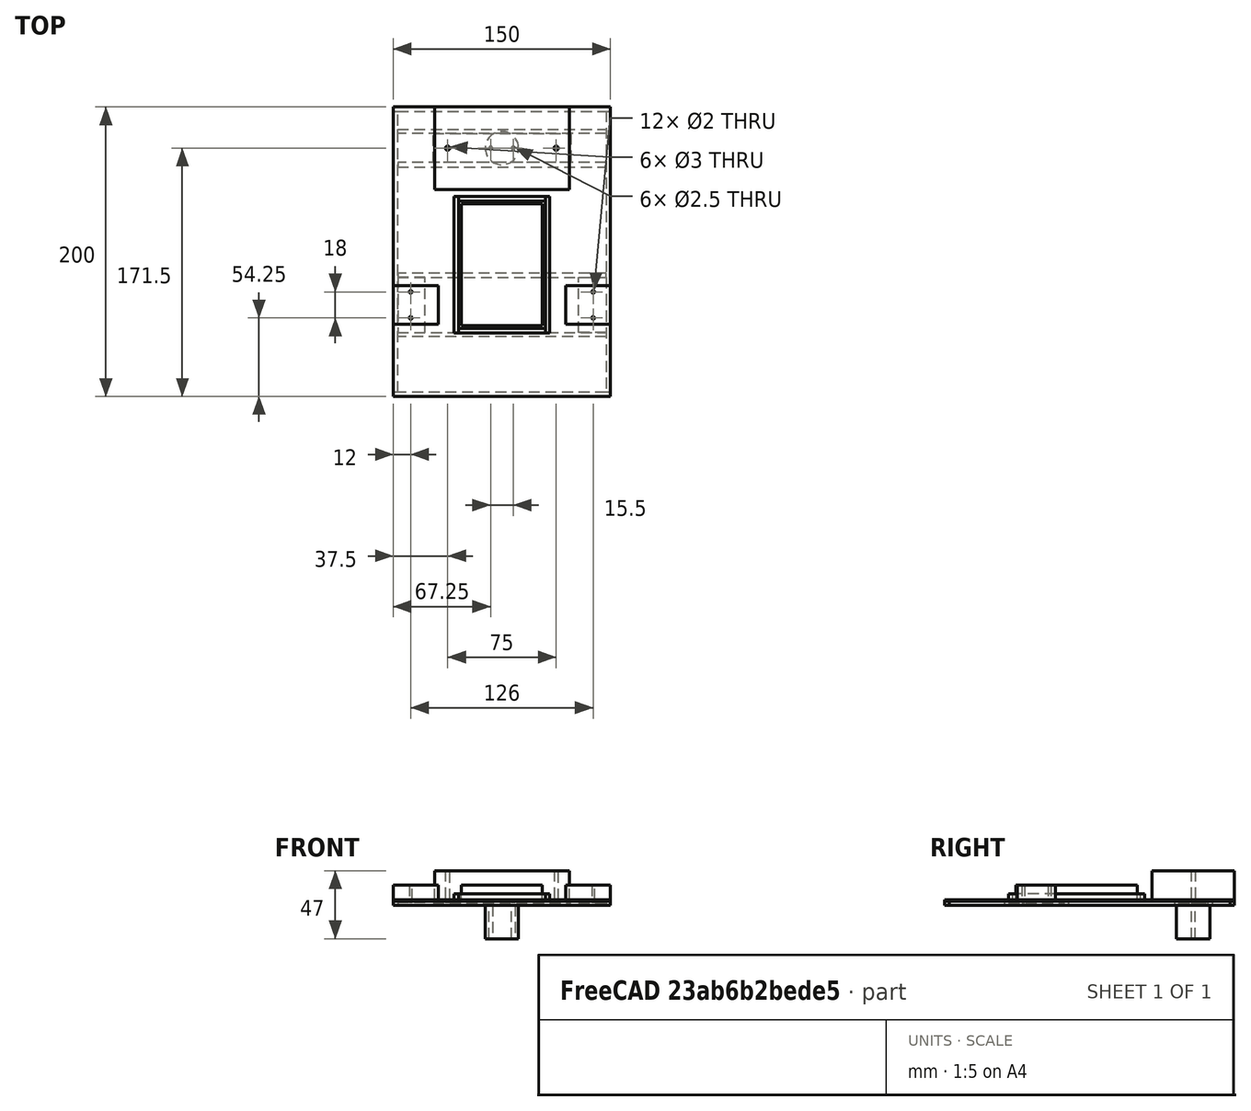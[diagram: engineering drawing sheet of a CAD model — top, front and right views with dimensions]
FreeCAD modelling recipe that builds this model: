
FCSTD DOCUMENT  (FreeCAD 0.20R26375 (Git))
Label: Robot
License: All rights reserved
LicenseURL: http://en.wikipedia.org/wiki/All_rights_reserved
objects: PartDesign::ShapeBinder×23, PartDesign::Pad×21, PartDesign::Body×21, TechDraw::DrawViewDimension×11, Sketcher::SketchObject×7, TechDraw::DrawProjGroupItem×5, TechDraw::DrawProjGroup×5, PartDesign::Pocket×3, TechDraw::DrawSVGTemplate×2, TechDraw::DrawPage×2
note: 99 computed .brp shape members not serialized (recipe doc carries the construction recipe); baked Part::Feature solids carry a one-line shape summary decoded from their .brp

FEATURE [Sketcher::SketchObject] Sketch  label="ChassisOutline"
  FullyConstrained = true
  MapMode = 5
  Support = -> [XY_Plane]
  sketch-geometry (4):
    g0: LineSegment StartX=-75 StartY=100 StartZ=0 EndX=75 EndY=100 EndZ=0
    g1: LineSegment StartX=75 StartY=100 StartZ=0 EndX=75 EndY=-100 EndZ=0
    g2: LineSegment StartX=75 StartY=-100 StartZ=0 EndX=-75 EndY=-100 EndZ=0
    g3: LineSegment StartX=-75 StartY=-100 StartZ=0 EndX=-75 EndY=100 EndZ=0
  constraints (11):
    c: Coincident(g0,g1)
    c: Coincident(g1,g2)
    c: Coincident(g2,g3)
    c: Coincident(g3,g0)
    c: Horizontal(g0)
    c: Horizontal(g2)
    c: Vertical(g1)
    c: Vertical(g3)
    c: Distance(g0) = 150
    c: Distance(g3) = 200
    c: Symmetric(g0,g1,g-1)
FEATURE [Sketcher::SketchObject] Sketch001  label="UpperParts"
  ExternalGeometry = -> [Sketch]
  FullyConstrained = true
  MapMode = 5
  Support = -> [XY_Plane]
  sketch-geometry (24):
    g0: LineSegment StartX=-46.5 StartY=100 StartZ=0 EndX=46.5 EndY=100 EndZ=0
    g1: LineSegment StartX=46.5 StartY=100 StartZ=0 EndX=46.5 EndY=43 EndZ=0
    g2: LineSegment StartX=46.5 StartY=43 StartZ=0 EndX=-46.5 EndY=43 EndZ=0
    g3: LineSegment StartX=-46.5 StartY=43 StartZ=0 EndX=-46.5 EndY=100 EndZ=0
    g4: LineSegment StartX=-28 StartY=33 StartZ=0 EndX=28 EndY=33 EndZ=0
    g5: LineSegment StartX=28 StartY=33 StartZ=0 EndX=28 EndY=-51 EndZ=0
    g6: LineSegment StartX=28 StartY=-51 StartZ=0 EndX=-28 EndY=-51 EndZ=0
    g7: LineSegment StartX=-28 StartY=-51 StartZ=0 EndX=-28 EndY=33 EndZ=0
    g8: LineSegment StartX=-44 StartY=-50 StartZ=0 EndX=-75 EndY=-50 EndZ=0
    g9: LineSegment StartX=-75 StartY=-50 StartZ=0 EndX=-75 EndY=-23.5 EndZ=0
    g10: LineSegment StartX=-75 StartY=-23.5 StartZ=0 EndX=-44 EndY=-23.5 EndZ=0
    g11: LineSegment StartX=-44 StartY=-23.5 StartZ=0 EndX=-44 EndY=-50 EndZ=0
    g12: LineSegment StartX=75 StartY=-23.5 StartZ=0 EndX=44 EndY=-23.5 EndZ=0
    g13: LineSegment StartX=44 StartY=-23.5 StartZ=0 EndX=44 EndY=-50 EndZ=0
    g14: LineSegment StartX=44 StartY=-50 StartZ=0 EndX=75 EndY=-50 EndZ=0
    g15: LineSegment StartX=75 StartY=-50 StartZ=0 EndX=75 EndY=-23.5 EndZ=0
    g16: LineSegment StartX=-37.5 StartY=71.5 StartZ=0 EndX=0 EndY=71.5 EndZ=0
    g17: Circle CenterX=-37.5 CenterY=71.5 CenterZ=0 NormalX=0 NormalY=0 NormalZ=1 AngleXU=0 Radius=1.5
    g18: Circle CenterX=37.5 CenterY=71.5 CenterZ=0 NormalX=0 NormalY=0 NormalZ=1 AngleXU=0 Radius=1.5
    g19: Circle CenterX=-63 CenterY=-27.75 CenterZ=0 NormalX=0 NormalY=0 NormalZ=1 AngleXU=0 Radius=1
    g20: Circle CenterX=-63 CenterY=-45.75 CenterZ=0 NormalX=0 NormalY=0 NormalZ=1 AngleXU=0 Radius=1
    g21: Circle CenterX=63 CenterY=-27.75 CenterZ=0 NormalX=0 NormalY=0 NormalZ=1 AngleXU=0 Radius=1
    g22: Circle CenterX=63 CenterY=-45.75 CenterZ=0 NormalX=0 NormalY=0 NormalZ=1 AngleXU=0 Radius=1
    g23: LineSegment StartX=-75 StartY=-36.75 StartZ=0 EndX=-44 EndY=-36.75 EndZ=0
  constraints (64):
    c: Coincident(g0,g1)
    c: Coincident(g1,g2)
    c: Coincident(g2,g3)
    c: Coincident(g3,g0)
    c: Horizontal(g0)
    c: Vertical(g1)
    c: Vertical(g3)
    c: PointOnObject(g0,g-3)
    c: Symmetric(g2,g1,g-2)
    c: Distance(g2) = 93
    c: Distance(g3) = 57
    c: Coincident(g4,g5)
    c: Coincident(g5,g6)
    c: Coincident(g6,g7)
    c: Coincident(g7,g4)
    c: Horizontal(g6)
    c: Vertical(g5)
    c: Vertical(g7)
    c: Symmetric(g4,g4,g-2)
    c: Distance(g4) = 56
    c: Distance(g7) = 84
    c: DistanceY(g4,g2) = 10
    c: Coincident(g8,g9)
    c: Coincident(g9,g10)
    c: Coincident(g10,g11)
    c: Coincident(g11,g8)
    c: Horizontal(g8)
    c: Horizontal(g10)
    c: Vertical(g9)
    c: Vertical(g11)
    c: PointOnObject(g9,g-4)
    c: Coincident(g12,g13)
    c: Coincident(g13,g14)
    c: Coincident(g14,g15)
    c: Coincident(g15,g12)
    c: Horizontal(g12)
    c: Horizontal(g14)
    c: Vertical(g13)
    c: Vertical(g15)
    c: PointOnObject(g12,g-6)
    c: Symmetric(g10,g12,g-2)
    c: Equal(g11,g13)
    c: Distance(g9) = 26.5
    c: Distance(g10) = 31
    c: Distance(g8,g-5) = 50
    c: PointOnObject(g16,g-2)
    c: Coincident(g17,g16)
    c: DistanceX(g17,g18) = 75
    c: Equal(g17,g18)
    c: Symmetric(g17,g18,g-2)
    c: Diameter(g18) = 3
    c: Symmetric(g0,g2,g16)
    c: PointOnObject(g23,g9)
    c: PointOnObject(g23,g11)
    c: Symmetric(g19,g20,g23)
    c: Distance(g20,g19) = 18
    c: Symmetric(g8,g9,g23)
    c: Symmetric(g20,g22,g-2)
    c: Symmetric(g19,g21,g-2)
    c: Equal(g21,g22)
    c: Equal(g22,g20)
    c: Equal(g20,g19)
    c: Diameter(g19) = 2
    c: DistanceX(g9,g19) = 12
FEATURE [PartDesign::Pad] Pad
  Direction = (0,0,1)
  Length = 1
  Length2 = 100
  Profile = -> Sketch
  Reversed = true
  Type = 0
FEATURE [PartDesign::ShapeBinder] ShapeBinder
  Support = -> [Sketch001]
  TraceSupport = false
FEATURE [PartDesign::Pocket] Pocket
  BaseFeature = -> Pad
  Direction = (1,1,1)
  Length = 5
  Length2 = 100
  Profile = -> ShapeBinder
  Type = 1
FEATURE [PartDesign::ShapeBinder] ShapeBinder001
  Support = -> [Sketch001]
  TraceSupport = false
FEATURE [PartDesign::Pad] Pad001
  Direction = (0,0,-1)
  Length = 20
  Length2 = 100
  Profile = -> ShapeBinder001
  Reversed = true
  Type = 0
FEATURE [PartDesign::Body] Body001  label="BatteryBox"
  Group = -> [ShapeBinder001,Pad001]
  Origin = -> Origin001
  Tip = -> Pad001
FEATURE [PartDesign::ShapeBinder] ShapeBinder002
  Support = -> [Sketch001]
  TraceSupport = false
FEATURE [PartDesign::Pad] Pad002
  Direction = (0,0,-1)
  Length = 10
  Length2 = 100
  Profile = -> ShapeBinder002
  Reversed = true
  Type = 0
FEATURE [PartDesign::Body] Body002  label="Breadboard"
  Group = -> [ShapeBinder002,Pad002]
  Origin = -> Origin002
  Tip = -> Pad002
FEATURE [PartDesign::ShapeBinder] ShapeBinder003
  Support = -> [Sketch001]
  TraceSupport = false
FEATURE [PartDesign::Pad] Pad003
  Direction = (0,0,-1)
  Length = 10
  Length2 = 100
  Profile = -> ShapeBinder003
  Reversed = true
  Type = 0
FEATURE [PartDesign::Body] Body003  label="LeftMotor"
  Group = -> [ShapeBinder003,Pad003]
  Origin = -> Origin003
  Tip = -> Pad003
FEATURE [PartDesign::ShapeBinder] ShapeBinder004
  Support = -> [Sketch001]
  TraceSupport = false
FEATURE [PartDesign::Pad] Pad004
  Direction = (0,0,1)
  Length = 10
  Length2 = 100
  Profile = -> ShapeBinder004
  Type = 0
FEATURE [PartDesign::Body] Body004  label="RightMotor"
  Group = -> [ShapeBinder004,Pad004]
  Origin = -> Origin004
  Tip = -> Pad004
FEATURE [Sketcher::SketchObject] Sketch002  label="OuterSupportRods"
  ExternalGeometry = -> [Pocket]
  FullyConstrained = true
  MapMode = 5
  Placement = pos=(0,0,-1) rot=(1,0,0;3.14159rad)
  Support = -> [Pocket]
  sketch-geometry (16):
    g0: LineSegment StartX=-75 StartY=100 StartZ=0 EndX=75 EndY=100 EndZ=0
    g1: LineSegment StartX=75 StartY=100 StartZ=0 EndX=75 EndY=97 EndZ=0
    g2: LineSegment StartX=-75 StartY=97 StartZ=0 EndX=-75 EndY=100 EndZ=0
    g3: LineSegment StartX=75 StartY=-100 StartZ=0 EndX=-75 EndY=-100 EndZ=0
    g4: LineSegment StartX=-75 StartY=-100 StartZ=0 EndX=-75 EndY=-97 EndZ=0
    g5: LineSegment StartX=75 StartY=-97 StartZ=0 EndX=75 EndY=-100 EndZ=0
    g6: LineSegment StartX=-72 StartY=97 StartZ=0 EndX=-75 EndY=97 EndZ=0
    g7: LineSegment StartX=75 StartY=97 StartZ=0 EndX=72 EndY=97 EndZ=0
    g8: LineSegment StartX=72 StartY=97 StartZ=0 EndX=-72 EndY=97 EndZ=0
    g9: LineSegment StartX=72 StartY=-97 StartZ=0 EndX=75 EndY=-97 EndZ=0
    g10: LineSegment StartX=-75 StartY=-97 StartZ=0 EndX=-72 EndY=-97 EndZ=0
    g11: LineSegment StartX=-72 StartY=-97 StartZ=0 EndX=72 EndY=-97 EndZ=0
    g12: LineSegment StartX=-75 StartY=97 StartZ=0 EndX=-75 EndY=-97 EndZ=0
    g13: LineSegment StartX=75 StartY=97 StartZ=0 EndX=75 EndY=-97 EndZ=0
    g14: LineSegment StartX=72 StartY=-97 StartZ=0 EndX=72 EndY=97 EndZ=0
    g15: LineSegment StartX=-72 StartY=97 StartZ=0 EndX=-72 EndY=-97 EndZ=0
  constraints (40):
    c: Coincident(g0,g1)
    c: Coincident(g1,g7)
    c: Coincident(g6,g2)
    c: Coincident(g2,g0)
    c: Vertical(g1)
    c: Vertical(g2)
    c: Coincident(g3,g4)
    c: Coincident(g4,g10)
    c: Coincident(g9,g5)
    c: Coincident(g5,g3)
    c: Vertical(g4)
    c: Vertical(g5)
    c: Equal(g2,g4)
    c: Distance(g2) = 3
    c: Coincident(g3,g-3)
    c: Coincident(g0,g-3)
    c: Coincident(g-4,g0)
    c: Coincident(g3,g-4)
    c: Coincident(g8,g6)
    c: Horizontal(g6)
    c: Coincident(g7,g8)
    c: Horizontal(g7)
    c: Horizontal(g8)
    c: Coincident(g11,g9)
    c: Horizontal(g9)
    c: Coincident(g10,g11)
    c: Horizontal(g10)
    c: Horizontal(g11)
    c: Equal(g6,g7)
    c: Equal(g6,g2)
    c: Coincident(g12,g2)
    c: Coincident(g12,g4)
    c: Coincident(g13,g1)
    c: Coincident(g13,g5)
    c: Coincident(g14,g9)
    c: Coincident(g14,g7)
    c: Coincident(g15,g6)
    c: Coincident(g15,g10)
    c: Vertical(g15)
    c: Vertical(g14)
FEATURE [PartDesign::ShapeBinder] ShapeBinder005
  Support = -> [Sketch002]
  TraceSupport = false
FEATURE [PartDesign::Pad] Pad005
  Direction = (0,0,1)
  Length = 3
  Length2 = 100
  Profile = -> ShapeBinder005
  Reversed = true
  Type = 0
FEATURE [PartDesign::Body] Body005  label="FrontRod"
  Group = -> [ShapeBinder005,Pad005]
  Origin = -> Origin005
  Tip = -> Pad005
FEATURE [PartDesign::ShapeBinder] ShapeBinder006
  Support = -> [Sketch002]
  TraceSupport = false
FEATURE [PartDesign::Pad] Pad006
  Direction = (0,0,1)
  Length = 3
  Length2 = 100
  Profile = -> ShapeBinder006
  Reversed = true
  Type = 0
FEATURE [PartDesign::Body] Body006  label="RearRod"
  Group = -> [ShapeBinder006,Pad006]
  Origin = -> Origin006
  Tip = -> Pad006
FEATURE [PartDesign::ShapeBinder] ShapeBinder007
  Support = -> [Sketch002]
  TraceSupport = false
FEATURE [PartDesign::Pad] Pad007
  Direction = (0,0,-1)
  Length = 3
  Length2 = 100
  Profile = -> ShapeBinder007
  Type = 0
FEATURE [PartDesign::Body] Body007  label="LeftRod"
  Group = -> [ShapeBinder007,Pad007]
  Origin = -> Origin007
  Tip = -> Pad007
FEATURE [PartDesign::ShapeBinder] ShapeBinder008
  Support = -> [Sketch002]
  TraceSupport = false
FEATURE [PartDesign::Pad] Pad008
  Direction = (0,0,1)
  Length = 3
  Length2 = 100
  Profile = -> ShapeBinder008
  Reversed = true
  Type = 0
FEATURE [PartDesign::Body] Body008  label="RightRod"
  Group = -> [ShapeBinder008,Pad008]
  Origin = -> Origin008
  Tip = -> Pad008
FEATURE [Sketcher::SketchObject] Sketch003  label="InnerSupportRods"
  ExternalGeometry = -> [Sketch002,Pocket]
  FullyConstrained = true
  MapMode = 5
  Placement = pos=(0,0,-1) rot=(1,0,0;3.14159rad)
  Support = -> [Pocket]
  sketch-geometry (16):
    g0: LineSegment StartX=-72 StartY=55.75 StartZ=0 EndX=72 EndY=55.75 EndZ=0
    g1: LineSegment StartX=72 StartY=55.75 StartZ=0 EndX=72 EndY=58.75 EndZ=0
    g2: LineSegment StartX=72 StartY=58.75 StartZ=0 EndX=-72 EndY=58.75 EndZ=0
    g3: LineSegment StartX=-72 StartY=58.75 StartZ=0 EndX=-72 EndY=55.75 EndZ=0
    g4: LineSegment StartX=-72 StartY=17.75 StartZ=0 EndX=72 EndY=17.75 EndZ=0
    g5: LineSegment StartX=72 StartY=17.75 StartZ=0 EndX=72 EndY=14.75 EndZ=0
    g6: LineSegment StartX=72 StartY=14.75 StartZ=0 EndX=-72 EndY=14.75 EndZ=0
    g7: LineSegment StartX=-72 StartY=14.75 StartZ=0 EndX=-72 EndY=17.75 EndZ=0
    g8: LineSegment StartX=-72 StartY=-58.5 StartZ=0 EndX=72 EndY=-58.5 EndZ=0
    g9: LineSegment StartX=72 StartY=-58.5 StartZ=0 EndX=72 EndY=-61.5 EndZ=0
    g10: LineSegment StartX=72 StartY=-61.5 StartZ=0 EndX=-72 EndY=-61.5 EndZ=0
    g11: LineSegment StartX=-72 StartY=-61.5 StartZ=0 EndX=-72 EndY=-58.5 EndZ=0
    g12: LineSegment StartX=72 StartY=-81.5 StartZ=0 EndX=-72 EndY=-81.5 EndZ=0
    g13: LineSegment StartX=-72 StartY=-81.5 StartZ=0 EndX=-72 EndY=-84.5 EndZ=0
    g14: LineSegment StartX=-72 StartY=-84.5 StartZ=0 EndX=72 EndY=-84.5 EndZ=0
    g15: LineSegment StartX=72 StartY=-84.5 StartZ=0 EndX=72 EndY=-81.5 EndZ=0
  constraints (48):
    c: Coincident(g0,g1)
    c: Coincident(g1,g2)
    c: Coincident(g2,g3)
    c: Coincident(g3,g0)
    c: Horizontal(g0)
    c: Horizontal(g2)
    c: Vertical(g1)
    c: Vertical(g3)
    c: PointOnObject(g0,g-4)
    c: PointOnObject(g1,g-5)
    c: Coincident(g4,g5)
    c: Coincident(g5,g6)
    c: Coincident(g6,g7)
    c: Coincident(g7,g4)
    c: Horizontal(g4)
    c: Horizontal(g6)
    c: Vertical(g5)
    c: Vertical(g7)
    c: PointOnObject(g4,g-4)
    c: PointOnObject(g5,g-5)
    c: Coincident(g8,g9)
    c: Coincident(g9,g10)
    c: Coincident(g10,g11)
    c: Coincident(g11,g8)
    c: Horizontal(g8)
    c: Horizontal(g10)
    c: Vertical(g9)
    c: Vertical(g11)
    c: PointOnObject(g8,g-4)
    c: PointOnObject(g9,g-5)
    c: Coincident(g12,g13)
    c: Coincident(g13,g14)
    c: Coincident(g14,g15)
    c: Coincident(g15,g12)
    c: Horizontal(g12)
    c: Horizontal(g14)
    c: Vertical(g13)
    c: Vertical(g15)
    c: PointOnObject(g12,g-5)
    c: PointOnObject(g13,g-4)
    c: Equal(g13,g11)
    c: Equal(g11,g7)
    c: Equal(g7,g3)
    c: Equal(g3,g-3)
    c: DistanceY(g-8,g0) = 10
    c: DistanceY(g4,g-9) = 10
    c: DistanceY(g-10,g10) = 10
    c: DistanceY(g12,g-10) = 10
FEATURE [Sketcher::SketchObject] Sketch004  label="SupportPlates"
  ExternalGeometry = -> [Sketch002,Sketch003,Pocket]
  FullyConstrained = true
  MapMode = 5
  Placement = pos=(0,0,-1) rot=(1,0,0;3.14159rad)
  Support = -> [Pocket]
  sketch-geometry (18):
    g0: Circle CenterX=-63 CenterY=45.75 CenterZ=0 NormalX=0 NormalY=0 NormalZ=1 AngleXU=0 Radius=1
    g1: Circle CenterX=-63 CenterY=27.75 CenterZ=0 NormalX=0 NormalY=0 NormalZ=1 AngleXU=0 Radius=1
    g2: Circle CenterX=63 CenterY=45.75 CenterZ=0 NormalX=0 NormalY=0 NormalZ=1 AngleXU=0 Radius=1
    g3: Circle CenterX=63 CenterY=27.75 CenterZ=0 NormalX=0 NormalY=0 NormalZ=1 AngleXU=0 Radius=1
    g4: Circle CenterX=-37.5 CenterY=-71.5 CenterZ=0 NormalX=0 NormalY=0 NormalZ=1 AngleXU=0 Radius=1.5
    g5: Circle CenterX=37.5 CenterY=-71.5 CenterZ=0 NormalX=0 NormalY=0 NormalZ=1 AngleXU=0 Radius=1.5
    g6: LineSegment StartX=-72 StartY=55.75 StartZ=0 EndX=-53 EndY=55.75 EndZ=0
    g7: LineSegment StartX=-53 StartY=55.75 StartZ=0 EndX=-53 EndY=17.75 EndZ=0
    g8: LineSegment StartX=-53 StartY=17.75 StartZ=0 EndX=-72 EndY=17.75 EndZ=0
    g9: LineSegment StartX=-72 StartY=17.75 StartZ=0 EndX=-72 EndY=55.75 EndZ=0
    g10: LineSegment StartX=72 StartY=55.75 StartZ=0 EndX=53 EndY=55.75 EndZ=0
    g11: LineSegment StartX=53 StartY=55.75 StartZ=0 EndX=53 EndY=17.75 EndZ=0
    g12: LineSegment StartX=53 StartY=17.75 StartZ=0 EndX=72 EndY=17.75 EndZ=0
    g13: LineSegment StartX=72 StartY=17.75 StartZ=0 EndX=72 EndY=55.75 EndZ=0
    g14: LineSegment StartX=47.5 StartY=-61.5 StartZ=0 EndX=-47.5 EndY=-61.5 EndZ=0
    g15: LineSegment StartX=-47.5 StartY=-61.5 StartZ=0 EndX=-47.5 EndY=-81.5 EndZ=0
    g16: LineSegment StartX=-47.5 StartY=-81.5 StartZ=0 EndX=47.5 EndY=-81.5 EndZ=0
    g17: LineSegment StartX=47.5 StartY=-81.5 StartZ=0 EndX=47.5 EndY=-61.5 EndZ=0
  constraints (44):
    c: Coincident(g0,g-9)
    c: Coincident(g1,g-10)
    c: Coincident(g2,g-7)
    c: Coincident(g3,g-8)
    c: Coincident(g4,g-13)
    c: Coincident(g5,g-14)
    c: Equal(g-10,g1)
    c: Equal(g0,g-9)
    c: Equal(g2,g-7)
    c: Equal(g3,g-8)
    c: Equal(g5,g-14)
    c: Equal(g4,g-13)
    c: Coincident(g6,g7)
    c: Coincident(g7,g8)
    c: Coincident(g8,g9)
    c: Coincident(g9,g6)
    c: Horizontal(g6)
    c: Horizontal(g8)
    c: Vertical(g7)
    c: Vertical(g9)
    c: Coincident(g6,g-5)
    c: PointOnObject(g7,g-6)
    c: Coincident(g10,g11)
    c: Coincident(g11,g12)
    c: Coincident(g12,g13)
    c: Coincident(g13,g10)
    c: Horizontal(g12)
    c: Vertical(g11)
    c: Vertical(g13)
    c: Coincident(g10,g-5)
    c: PointOnObject(g11,g-6)
    c: Coincident(g14,g15)
    c: Coincident(g15,g16)
    c: Coincident(g16,g17)
    c: Coincident(g17,g14)
    c: Horizontal(g16)
    c: Vertical(g15)
    c: Vertical(g17)
    c: PointOnObject(g14,g-11)
    c: PointOnObject(g15,g-12)
    c: Symmetric(g6,g10,g-2)
    c: Symmetric(g14,g14,g-2)
    c: DistanceX(g0,g6) = 10
    c: DistanceX(g14,g4) = 10
FEATURE [PartDesign::ShapeBinder] ShapeBinder009
  Support = -> [Sketch003]
  TraceSupport = false
FEATURE [PartDesign::Pad] Pad009
  Direction = (0,0,-1)
  Length = 3
  Length2 = 100
  Profile = -> ShapeBinder009
  Type = 0
FEATURE [PartDesign::Body] Body009  label="MotorFrontRod"
  Group = -> [ShapeBinder009,Pad009]
  Origin = -> Origin009
  Tip = -> Pad009
FEATURE [PartDesign::ShapeBinder] ShapeBinder010
  Support = -> [Sketch003]
  TraceSupport = false
FEATURE [PartDesign::Pad] Pad010
  Direction = (0,0,-1)
  Length = 3
  Length2 = 100
  Profile = -> ShapeBinder010
  Type = 0
FEATURE [PartDesign::Body] Body010  label="BatteryRearRod"
  Group = -> [ShapeBinder010,Pad010]
  Origin = -> Origin010
  Tip = -> Pad010
FEATURE [PartDesign::ShapeBinder] ShapeBinder011
  Support = -> [Sketch003]
  TraceSupport = false
FEATURE [PartDesign::Pad] Pad011
  Direction = (0,0,1)
  Length = 3
  Length2 = 100
  Profile = -> ShapeBinder011
  Reversed = true
  Type = 0
FEATURE [PartDesign::Body] Body011  label="BatteryFrontRod"
  Group = -> [ShapeBinder011,Pad011]
  Origin = -> Origin011
  Tip = -> Pad011
FEATURE [PartDesign::ShapeBinder] ShapeBinder012
  Support = -> [Sketch003]
  TraceSupport = false
FEATURE [PartDesign::Pad] Pad012
  Direction = (0,0,1)
  Length = 3
  Length2 = 100
  Profile = -> ShapeBinder012
  Reversed = true
  Type = 0
FEATURE [PartDesign::Body] Body012  label="MotorRearRod"
  Group = -> [ShapeBinder012,Pad012]
  Origin = -> Origin012
  Tip = -> Pad012
FEATURE [PartDesign::ShapeBinder] ShapeBinder013
  Support = -> [Sketch004]
  TraceSupport = false
FEATURE [PartDesign::Pad] Pad013
  Direction = (0,0,-1)
  Length = 1
  Length2 = 100
  Profile = -> ShapeBinder013
  Type = 0
FEATURE [PartDesign::ShapeBinder] ShapeBinder014
  Support = -> [Sketch004]
  TraceSupport = false
FEATURE [PartDesign::Pad] Pad014
  Direction = (0,0,-1)
  Length = 1
  Length2 = 100
  Profile = -> ShapeBinder014
  Type = 0
FEATURE [PartDesign::Body] Body014  label="RightMotorPlate"
  Group = -> [ShapeBinder014,Pad014]
  Origin = -> Origin014
  Tip = -> Pad014
FEATURE [PartDesign::ShapeBinder] ShapeBinder015
  Support = -> [Sketch004]
  TraceSupport = false
FEATURE [PartDesign::Pad] Pad015
  Direction = (0,0,1)
  Length = 1
  Length2 = 100
  Profile = -> ShapeBinder015
  Reversed = true
  Type = 0
FEATURE [PartDesign::Body] Body015  label="LeftMotorPlate"
  Group = -> [ShapeBinder015,Pad015]
  Origin = -> Origin015
  Tip = -> Pad015
FEATURE [Sketcher::SketchObject] Sketch005  label="CastorSketch"
  ExternalGeometry = -> [Pocket]
  FullyConstrained = true
  MapMode = 5
  Placement = pos=(0,0,-1) rot=(1,0,0;3.14159rad)
  Support = -> [Pocket]
  sketch-geometry (4):
    g0: LineSegment StartX=-37.5 StartY=-71.5 StartZ=0 EndX=0 EndY=-71.5 EndZ=0
    g1: Circle CenterX=-7.75 CenterY=-71.5 CenterZ=0 NormalX=0 NormalY=0 NormalZ=1 AngleXU=0 Radius=1.25
    g2: Circle CenterX=7.75 CenterY=-71.5 CenterZ=0 NormalX=0 NormalY=0 NormalZ=1 AngleXU=0 Radius=1.25
    g3: Circle CenterX=0 CenterY=-71.5 CenterZ=0 NormalX=0 NormalY=0 NormalZ=1 AngleXU=0 Radius=11.5
  constraints (10):
    c: Coincident(g0,g-3)
    c: PointOnObject(g0,g-2)
    c: Horizontal(g0)
    c: PointOnObject(g1,g0)
    c: Equal(g1,g2)
    c: Symmetric(g1,g2,g-2)
    c: Distance(g1,g2) = 15.5
    c: Diameter(g1) = 2.5
    c: Coincident(g3,g0)
    c: Diameter(g3) = 23
FEATURE [PartDesign::ShapeBinder] ShapeBinder016
  Support = -> [Sketch005]
  TraceSupport = false
FEATURE [PartDesign::Pocket] Pocket001
  BaseFeature = -> Pocket
  Direction = (1,1,1)
  Length = 5
  Length2 = 100
  Profile = -> ShapeBinder016
  Reversed = true
  Type = 1
FEATURE [PartDesign::ShapeBinder] ShapeBinder017
  Support = -> [Sketch005]
  TraceSupport = false
FEATURE [PartDesign::Pocket] Pocket002
  BaseFeature = -> Pad013
  Direction = (1,1,1)
  Length = 5
  Length2 = 100
  Profile = -> ShapeBinder017
  Type = 1
FEATURE [PartDesign::Body] Body013  label="BatteryPlate"
  Group = -> [ShapeBinder013,Pad013,ShapeBinder017,Pocket002]
  Origin = -> Origin013
  Tip = -> Pocket002
FEATURE [PartDesign::ShapeBinder] ShapeBinder018
  Support = -> [Sketch005]
  TraceSupport = false
FEATURE [PartDesign::Pad] Pad016
  Direction = (0,0,-1)
  Length = 23
  Length2 = 100
  Profile = -> ShapeBinder018
  Type = 0
FEATURE [PartDesign::Body] Body016  label="Castor"
  Group = -> [ShapeBinder018,Pad016]
  Origin = -> Origin016
  Placement = pos=(0,0,-3) rot=(0,0,1;0rad)
  Tip = -> Pad016
FEATURE [TechDraw::DrawSVGTemplate] Template003  label="Template"
  Height = 297
  Orientation = 0
  Width = 210
FEATURE [TechDraw::DrawProjGroupItem] ProjItem007  label="Front002"
  CoarseView = false
  Direction = (0,0,-1)
  Focus = 100
  HardHidden = false
  IsoCount = 0
  IsoHidden = false
  IsoVisible = false
  LockPosition = true
  Perspective = false
  Rotation = 0
  RotationVector = (1,0,0)
  ScaleType = 2
  SeamHidden = false
  SeamVisible = true
  SmoothHidden = false
  SmoothVisible = true
  Source = -> [Body013]
  Type = 0
  X = 0
  XDirection = (1e-16,1,0)
  Y = 0
FEATURE [TechDraw::DrawProjGroup] ProjGroup007  label="ProjGroup002"
  Anchor = -> ProjItem007
  AutoDistribute = true
  LockPosition = false
  ProjectionType = 0
  Rotation = 0
  ScaleType = 0
  Source = -> [Body013]
  Views = -> [ProjItem007]
  X = 28.3326
  Y = 235.758
  spacingX = 15
  spacingY = 15
FEATURE [TechDraw::DrawProjGroupItem] ProjItem008  label="Front003"
  CoarseView = false
  Direction = (0,0,-1)
  Focus = 100
  HardHidden = false
  IsoCount = 0
  IsoHidden = false
  IsoVisible = false
  LockPosition = true
  Perspective = false
  Rotation = 0
  RotationVector = (1,0,0)
  ScaleType = 2
  SeamHidden = false
  SeamVisible = true
  SmoothHidden = false
  SmoothVisible = true
  Source = -> [Body014]
  Type = 0
  X = 0
  XDirection = (1,0,0)
  Y = 0
FEATURE [TechDraw::DrawProjGroup] ProjGroup008  label="ProjGroup003"
  Anchor = -> ProjItem008
  AutoDistribute = true
  LockPosition = false
  ProjectionType = 0
  Rotation = 0
  ScaleType = 0
  Source = -> [Body014]
  Views = -> [ProjItem008]
  X = 28.3326
  Y = 156.788
  spacingX = 15
  spacingY = 15
FEATURE [TechDraw::DrawProjGroupItem] ProjItem009  label="Front004"
  CoarseView = false
  Direction = (0,0,-1)
  Focus = 100
  HardHidden = false
  IsoCount = 0
  IsoHidden = false
  IsoVisible = false
  LockPosition = true
  Perspective = false
  Rotation = 0
  RotationVector = (1,0,0)
  ScaleType = 2
  SeamHidden = false
  SeamVisible = true
  SmoothHidden = false
  SmoothVisible = true
  Source = -> [Body015]
  Type = 0
  X = 0
  XDirection = (1,0,0)
  Y = 0
FEATURE [TechDraw::DrawProjGroup] ProjGroup009  label="ProjGroup004"
  Anchor = -> ProjItem009
  AutoDistribute = true
  LockPosition = false
  ProjectionType = 0
  Rotation = 0
  ScaleType = 0
  Source = -> [Body015]
  Views = -> [ProjItem009]
  X = 28.5628
  Y = 104.526
  spacingX = 15
  spacingY = 15
FEATURE [TechDraw::DrawViewDimension] Dimension017
  Arbitrary = false
  ArbitraryTolerances = false
  EqualTolerance = true
  FormatSpec = ⌀%.2f
  FormatSpecOverTolerance = %+.2f
  FormatSpecUnderTolerance = %+.2f
  Inverted = false
  LockPosition = false
  MeasureType = 1
  OverTolerance = 0
  References2D = -> [ProjItem007]
  Rotation = 0
  ScaleType = 0
  TheoreticalExact = false
  Type = 5
  UnderTolerance = 0
  X = 6.56075
  Y = -24.9813
FEATURE [TechDraw::DrawViewDimension] Dimension018
  Arbitrary = false
  ArbitraryTolerances = false
  EqualTolerance = true
  FormatSpec = ⌀%.2f
  FormatSpecOverTolerance = %+.2f
  FormatSpecUnderTolerance = %+.2f
  Inverted = false
  LockPosition = false
  MeasureType = 1
  OverTolerance = 0
  References2D = -> [ProjItem007]
  Rotation = 0
  ScaleType = 0
  TheoreticalExact = false
  Type = 5
  UnderTolerance = 0
  X = 10.5981
  Y = 1.76635
FEATURE [TechDraw::DrawViewDimension] Dimension019
  Arbitrary = false
  ArbitraryTolerances = false
  EqualTolerance = true
  FormatSpec = ⌀%.2f
  FormatSpecOverTolerance = %+.2f
  FormatSpecUnderTolerance = %+.2f
  Inverted = false
  LockPosition = false
  MeasureType = 1
  OverTolerance = 0
  References2D = -> [ProjItem009]
  Rotation = 0
  ScaleType = 0
  TheoreticalExact = false
  Type = 5
  UnderTolerance = 0
  X = 13.2772
  Y = 17.7562
FEATURE [TechDraw::DrawViewDimension] Dimension020
  Arbitrary = false
  ArbitraryTolerances = false
  EqualTolerance = true
  FormatSpec = ⌀%.2f
  FormatSpecOverTolerance = %+.2f
  FormatSpecUnderTolerance = %+.2f
  Inverted = false
  LockPosition = false
  MeasureType = 1
  OverTolerance = 0
  References2D = -> [ProjItem008]
  Rotation = 0
  ScaleType = 0
  TheoreticalExact = false
  Type = 5
  UnderTolerance = 0
  X = 15.8366
  Y = 21.7553
FEATURE [Sketcher::SketchObject] Sketch006
  ExternalGeometry = -> [Sketch001]
  FullyConstrained = true
  MapMode = 5
  Support = -> [XY_Plane]
  sketch-geometry (16):
    g0: LineSegment StartX=-30 StartY=35 StartZ=0 EndX=30 EndY=35 EndZ=0
    g1: LineSegment StartX=30 StartY=35 StartZ=0 EndX=30 EndY=-53 EndZ=0
    g2: LineSegment StartX=30 StartY=-53 StartZ=0 EndX=-30 EndY=-53 EndZ=0
    g3: LineSegment StartX=-30 StartY=-53 StartZ=0 EndX=-30 EndY=35 EndZ=0
    g4: LineSegment StartX=33 StartY=38 StartZ=0 EndX=33 EndY=-56 EndZ=0
    g5: LineSegment StartX=-33 StartY=-56 StartZ=0 EndX=-33 EndY=38 EndZ=0
    g6: LineSegment StartX=-30 StartY=35 StartZ=0 EndX=-30 EndY=38 EndZ=0
    g7: LineSegment StartX=30 StartY=35 StartZ=0 EndX=30 EndY=38 EndZ=0
    g8: LineSegment StartX=-30 StartY=-53 StartZ=0 EndX=-30 EndY=-56 EndZ=0
    g9: LineSegment StartX=30 StartY=-53 StartZ=0 EndX=30 EndY=-56 EndZ=0
    g10: LineSegment StartX=-33 StartY=38 StartZ=0 EndX=-30 EndY=38 EndZ=0
    g11: LineSegment StartX=-30 StartY=38 StartZ=0 EndX=30 EndY=38 EndZ=0
    g12: LineSegment StartX=30 StartY=38 StartZ=0 EndX=33 EndY=38 EndZ=0
    g13: LineSegment StartX=33 StartY=-56 StartZ=0 EndX=30 EndY=-56 EndZ=0
    g14: LineSegment StartX=30 StartY=-56 StartZ=0 EndX=-30 EndY=-56 EndZ=0
    g15: LineSegment StartX=-30 StartY=-56 StartZ=0 EndX=-33 EndY=-56 EndZ=0
  constraints (39):
    c: Coincident(g0,g1)
    c: Coincident(g1,g2)
    c: Coincident(g2,g3)
    c: Coincident(g3,g0)
    c: Horizontal(g2)
    c: Vertical(g1)
    c: Vertical(g3)
    c: DistanceX(g-4,g0) = 2
    c: DistanceY(g-4,g0) = 2
    c: Symmetric(g0,g0,g-2)
    c: DistanceY(g1,g-5) = 2
    c: Coincident(g12,g4)
    c: Coincident(g4,g13)
    c: Coincident(g15,g5)
    c: Coincident(g5,g10)
    c: Vertical(g4)
    c: Vertical(g5)
    c: Symmetric(g12,g10,g-2)
    c: DistanceX(g0,g12) = 3
    c: DistanceY(g0,g12) = 3
    c: DistanceY(g4,g1) = 3
    c: Coincident(g6,g0)
    c: Vertical(g6)
    c: Coincident(g7,g0)
    c: Vertical(g7)
    c: Coincident(g8,g2)
    c: Vertical(g8)
    c: Coincident(g9,g1)
    c: Vertical(g9)
    c: Tangent(g11,g12) = -1.5708
    c: Tangent(g10,g11) = -1.5708
    c: Coincident(g6,g10)
    c: Coincident(g11,g7)
    c: Coincident(g13,g14)
    c: Horizontal(g13)
    c: Coincident(g13,g9)
    c: Horizontal(g14)
    c: Tangent(g14,g15) = -1.5708
    c: Coincident(g14,g8)
FEATURE [PartDesign::Body] Body  label="ChassisPlate"
  Group = -> [Sketch,Sketch001,Pad,ShapeBinder,Pocket,Sketch002,Sketch003,Sketch004,Sketch005,ShapeBinder016,Pocket001,Sketch006]
  Origin = -> Origin
  Tip = -> Pocket001
FEATURE [TechDraw::DrawProjGroupItem] ProjItem006  label="Front001"
  CoarseView = false
  Direction = (0,0,-1)
  Focus = 100
  HardHidden = false
  IsoCount = 0
  IsoHidden = false
  IsoVisible = false
  LockPosition = true
  Perspective = false
  Rotation = 0
  RotationVector = (1,0,0)
  ScaleType = 2
  SeamHidden = false
  SeamVisible = true
  SmoothHidden = false
  SmoothVisible = true
  Source = -> [Body]
  Type = 0
  X = 0
  XDirection = (1,0,0)
  Y = 0
FEATURE [TechDraw::DrawProjGroup] ProjGroup006  label="ProjGroup001"
  Anchor = -> ProjItem006
  AutoDistribute = true
  LockPosition = false
  ProjectionType = 0
  Rotation = 0
  ScaleType = 0
  Source = -> [Body]
  Views = -> [ProjItem006]
  X = 127.793
  Y = 183.726
  spacingX = 15
  spacingY = 15
FEATURE [TechDraw::DrawViewDimension] Dimension
  Arbitrary = false
  ArbitraryTolerances = false
  EqualTolerance = true
  FormatSpec = ⌀%.2f
  FormatSpecOverTolerance = %+.2f
  FormatSpecUnderTolerance = %+.2f
  Inverted = false
  LockPosition = false
  MeasureType = 1
  OverTolerance = 0
  References2D = -> [ProjItem006]
  Rotation = 0
  ScaleType = 0
  TheoreticalExact = false
  Type = 5
  UnderTolerance = 0
  X = -52.486
  Y = 35.5794
FEATURE [TechDraw::DrawViewDimension] Dimension015
  Arbitrary = false
  ArbitraryTolerances = false
  EqualTolerance = true
  FormatSpec = ⌀%.2f
  FormatSpecOverTolerance = %+.2f
  FormatSpecUnderTolerance = %+.2f
  Inverted = false
  LockPosition = false
  MeasureType = 1
  OverTolerance = 0
  References2D = -> [ProjItem006]
  Rotation = 0
  ScaleType = 0
  TheoreticalExact = false
  Type = 5
  UnderTolerance = 0
  X = 17.2472
  Y = -51.0448
FEATURE [TechDraw::DrawViewDimension] Dimension016
  Arbitrary = false
  ArbitraryTolerances = false
  EqualTolerance = true
  FormatSpec = ⌀%.2f
  FormatSpecOverTolerance = %+.2f
  FormatSpecUnderTolerance = %+.2f
  Inverted = false
  LockPosition = false
  MeasureType = 1
  OverTolerance = 0
  References2D = -> [ProjItem006]
  Rotation = 0
  ScaleType = 0
  TheoreticalExact = false
  Type = 5
  UnderTolerance = 0
  X = 46.4299
  Y = -55.0093
FEATURE [TechDraw::DrawPage] Page003  label="CuttingLayout"
  KeepUpdated = true
  NextBalloonIndex = 1
  ProjectionType = 0
  Template = -> Template003
  Views = -> [ProjGroup006,ProjGroup007,ProjGroup008,ProjGroup009,Dimension,Dimension015,Dimension016,Dimension017,Dimension018,Dimension019,Dimension020]
FEATURE [PartDesign::ShapeBinder] ShapeBinder019
  Support = -> [Sketch006]
  TraceSupport = false
FEATURE [PartDesign::Pad] Pad017
  Direction = (0,0,-1)
  Length = 4
  Length2 = 100
  Profile = -> ShapeBinder019
  Reversed = true
  Type = 0
FEATURE [PartDesign::Body] Body017  label="BreadboardRightRod"
  Group = -> [ShapeBinder019,Pad017]
  Origin = -> Origin017
  Tip = -> Pad017
FEATURE [PartDesign::ShapeBinder] ShapeBinder020
  Support = -> [Sketch006]
  TraceSupport = false
FEATURE [PartDesign::Pad] Pad018
  Direction = (0,0,-1)
  Length = 4
  Length2 = 100
  Profile = -> ShapeBinder020
  Reversed = true
  Type = 0
FEATURE [PartDesign::Body] Body018  label="BreadboardFrontRod"
  Group = -> [ShapeBinder020,Pad018]
  Origin = -> Origin018
  Tip = -> Pad018
FEATURE [PartDesign::ShapeBinder] ShapeBinder021
  Support = -> [Sketch006]
  TraceSupport = false
FEATURE [PartDesign::Pad] Pad019
  Direction = (0,0,1)
  Length = 4
  Length2 = 100
  Profile = -> ShapeBinder021
  Type = 0
FEATURE [PartDesign::Body] Body019  label="BreadboardLeftRod"
  Group = -> [ShapeBinder021,Pad019]
  Origin = -> Origin019
  Tip = -> Pad019
FEATURE [PartDesign::ShapeBinder] ShapeBinder022
  Support = -> [Sketch006]
  TraceSupport = false
FEATURE [PartDesign::Pad] Pad020
  Direction = (0,0,1)
  Length = 4
  Length2 = 100
  Profile = -> ShapeBinder022
  Type = 0
FEATURE [PartDesign::Body] Body020  label="BreadboardRearRod"
  Group = -> [ShapeBinder022,Pad020]
  Origin = -> Origin020
  Tip = -> Pad020
FEATURE [TechDraw::DrawSVGTemplate] Template  label="Template001"
  Height = 297
  Orientation = 0
  Width = 210
FEATURE [TechDraw::DrawProjGroupItem] ProjItem  label="Front"
  CoarseView = false
  Direction = (0,0,1)
  Focus = 100
  HardHidden = false
  IsoCount = 0
  IsoHidden = false
  IsoVisible = false
  LockPosition = true
  Perspective = false
  Rotation = 0
  RotationVector = (-1,0,0)
  ScaleType = 2
  SeamHidden = false
  SeamVisible = true
  SmoothHidden = false
  SmoothVisible = true
  Source = -> [Body,Body019,Body018,Body017,Body020]
  Type = 0
  X = 0
  XDirection = (-1,0,0)
  Y = 0
FEATURE [TechDraw::DrawProjGroup] ProjGroup
  Anchor = -> ProjItem
  AutoDistribute = true
  LockPosition = false
  ProjectionType = 0
  Rotation = 0
  ScaleType = 0
  Source = -> [Body,Body019,Body018,Body017,Body020]
  Views = -> [ProjItem]
  X = 111.096
  Y = 157.442
  spacingX = 15
  spacingY = 15
FEATURE [TechDraw::DrawViewDimension] Dimension021
  Arbitrary = false
  ArbitraryTolerances = false
  EqualTolerance = true
  FormatSpec = %.2f
  FormatSpecOverTolerance = %+.2f
  FormatSpecUnderTolerance = %+.2f
  Inverted = false
  LockPosition = false
  MeasureType = 1
  OverTolerance = 0
  References2D = -> [ProjItem]
  Rotation = 0
  ScaleType = 0
  TheoreticalExact = false
  Type = 2
  UnderTolerance = 0
  X = 39.6273
  Y = 9.51157
FEATURE [TechDraw::DrawViewDimension] Dimension022
  Arbitrary = false
  ArbitraryTolerances = false
  EqualTolerance = true
  FormatSpec = %.2f
  FormatSpecOverTolerance = %+.2f
  FormatSpecUnderTolerance = %+.2f
  Inverted = false
  LockPosition = false
  MeasureType = 1
  OverTolerance = 0
  References2D = -> [ProjItem]
  Rotation = 0
  ScaleType = 0
  TheoreticalExact = false
  Type = 1
  UnderTolerance = 0
  X = 0
  Y = 72.6882
FEATURE [TechDraw::DrawViewDimension] Dimension023
  Arbitrary = false
  ArbitraryTolerances = false
  EqualTolerance = true
  FormatSpec = %.2f
  FormatSpecOverTolerance = %+.2f
  FormatSpecUnderTolerance = %+.2f
  Inverted = false
  LockPosition = false
  MeasureType = 1
  OverTolerance = 0
  References2D = -> [ProjItem]
  Rotation = 0
  ScaleType = 0
  TheoreticalExact = false
  Type = 2
  UnderTolerance = 0
  X = -39.1202
  Y = 80.2844
FEATURE [TechDraw::DrawViewDimension] Dimension024
  Arbitrary = false
  ArbitraryTolerances = false
  EqualTolerance = true
  FormatSpec = %.2f
  FormatSpecOverTolerance = %+.2f
  FormatSpecUnderTolerance = %+.2f
  Inverted = false
  LockPosition = false
  MeasureType = 1
  OverTolerance = 0
  References2D = -> [ProjItem]
  Rotation = 0
  ScaleType = 0
  TheoreticalExact = false
  Type = 1
  UnderTolerance = 0
  X = -57.2757
  Y = -17.1509
FEATURE [TechDraw::DrawPage] Page  label="BreadboardRodGluingGuide"
  KeepUpdated = true
  NextBalloonIndex = 1
  ProjectionType = 0
  Template = -> Template
  Views = -> [ProjGroup,Dimension021,Dimension022,Dimension023,Dimension024]
